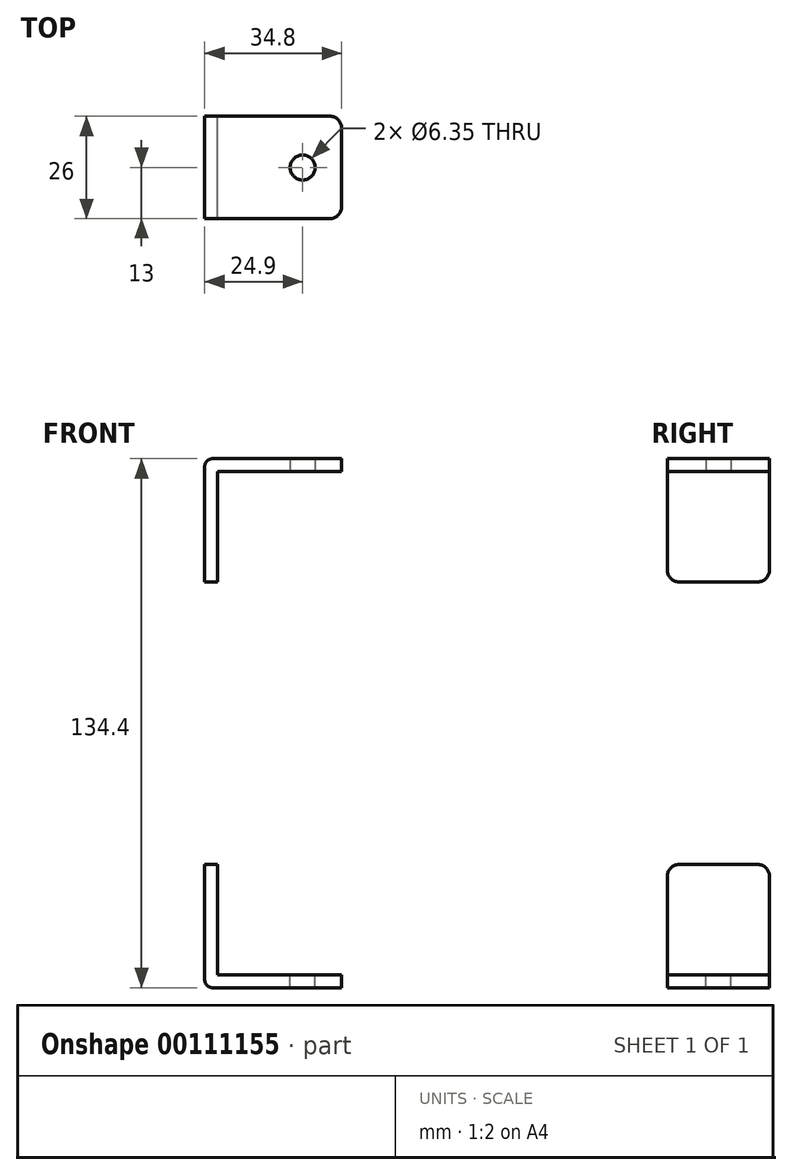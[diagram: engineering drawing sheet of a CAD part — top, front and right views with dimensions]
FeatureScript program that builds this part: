
annotation { "Feature Type Name" : "Feature", "Feature Type Description" : "" }
export const myFeature = defineFeature(function(context is Context, id is Id, definition is map)
    precondition{}
    {
        {
            var Q0;
            Q0=qCreatedBy(makeId("Top.planeOp"),FACE);
            var sketch = newSketch(context, id + "F0", { "sketchPlane" : qUnion([Q0])});
            skLineSegment(sketch, "E0.rect.bottom", {"start": v(15.75, 13) * mm, "end": v(-15.75, 13) * mm});
            skLineSegment(sketch, "E0.rect.top", {"start": v(15.75, -13) * mm, "end": v(-15.75, -13) * mm});
            skLineSegment(sketch, "E0.rect.left", {"start": v(15.75, 13) * mm, "end": v(15.75, -13) * mm});
            skLineSegment(sketch, "E0.rect.right", {"start": v(-15.75, 13) * mm, "end": v(-15.75, -13) * mm});
            skPoint(sketch, "E0.rect.middle", {"position": v(0, 0) * mm});
            skLineSegment(sketch, "E1.bottom", {"start": v(-15.75, 13) * mm, "end": v(-19.05, 13) * mm});
            skLineSegment(sketch, "E1.top", {"start": v(-15.75, -13) * mm, "end": v(-19.05, -13) * mm});
            skLineSegment(sketch, "E1.right", {"start": v(-19.05, 13) * mm, "end": v(-19.05, -13) * mm});
            skLineSegment(sketch, "E2", {"start": v(-15.75, 0) * mm, "end": v(15.75, 0) * mm, "construction": true});
            skSolve(sketch);
        }
        {
            var Q0;
            Q0=makeQuery(id+"F0.imprint","IMPRINT",FACE,{"disambiguationData":[TD([[makeQuery(id+"F0.imprint","IMPRINT",EDGE,{"derivedFrom":sQuery(id+"F0.wireOp",EDGE,"E1.bottom")}),1.0]])]});
            var Q1;
            Q1=makeQuery(id+"F0.imprint","IMPRINT",FACE,{"disambiguationData":[TD([[makeQuery(id+"F0.imprint","IMPRINT",EDGE,{"derivedFrom":sQuery(id+"F0.wireOp",EDGE,"E0.rect.bottom")}),1.0]])]});
            extrude(context, id + "F1", {"entities" : qUnion([Q0, Q1]), "oppositeDirection" : true, "depth" : 3.3 * mm});
        }
        {
            var Q0;
            Q0=makeQuery(id+"F0.imprint","IMPRINT",FACE,{"disambiguationData":[TD([[makeQuery(id+"F0.imprint","IMPRINT",EDGE,{"derivedFrom":sQuery(id+"F0.wireOp",EDGE,"E1.bottom")}),1.0]])]});
            extrude(context, id + "F2", {"entities" : qUnion([Q0]), "operationType" : NewBodyOperationType.ADD, "depth" : 28 * mm});
        }
        {
            var Q0;
            Q0=makeQuery(id+"F0.imprint","IMPRINT",FACE,{"disambiguationData":[TD([[makeQuery(id+"F0.imprint","IMPRINT",EDGE,{"derivedFrom":sQuery(id+"F0.wireOp",EDGE,"E0.rect.bottom")}),1.0]])]});
            var sketch = newSketch(context, id + "F3", { "sketchPlane" : qUnion([Q0])});
            skCircle(sketch, "E3", {"center": v(5.85, 0) * mm, "radius": 3.18 * mm});
            skSolve(sketch);
        }
        {
            var Q0;
            Q0=makeQuery(id+"F3.imprint","IMPRINT",FACE,{"disambiguationData":[TD([[makeQuery(id+"F3.imprint","IMPRINT",EDGE,{"derivedFrom":sQuery(id+"F3.wireOp",EDGE,"E3")}),1.0]])]});
            extrude(context, id + "F4", {"entities" : qUnion([Q0]), "operationType" : NewBodyOperationType.REMOVE, "endBound" : BoundingType.THROUGH_ALL, "oppositeDirection" : true, "depth" : 25 * mm});
        }
        {
            var Q0;
            Q0=makeQuery(id+"F1.opExtrude","SWEPT_EDGE",EDGE,{"disambiguationData":[OSD([sQuery(id+"F0.wireOp",EDGE,"E0.rect.top"),sQuery(id+"F0.wireOp",EDGE,"E0.rect.left")])]});
            var Q1;
            Q1=makeQuery(id+"F1.opExtrude","SWEPT_EDGE",EDGE,{"disambiguationData":[OSD([sQuery(id+"F0.wireOp",EDGE,"E0.rect.bottom"),sQuery(id+"F0.wireOp",EDGE,"E0.rect.left")])]});
            var Q2;
            Q2=makeQuery(id+"F2.opExtrude","CAP_EDGE",EDGE,{"disambiguationData":[OSD([sQuery(id+"F0.wireOp",EDGE,"E1.top")])],"isStart":false});
            var Q3;
            Q3=makeQuery(id+"F2.opExtrude","CAP_EDGE",EDGE,{"disambiguationData":[OSD([sQuery(id+"F0.wireOp",EDGE,"E1.bottom")])],"isStart":false});
            fillet(context, id + "F5", {"entities" : qUnion([Q0, Q1, Q2, Q3]), "radius" : 3 * mm, "tangentPropagation" : true, "allowEdgeOverflow" : false});
        }
        {
            var Q0;
            Q0=makeQuery(id+"F2.opExtrude","CAP_EDGE",EDGE,{"disambiguationData":[OSD([sQuery(id+"F0.wireOp",EDGE,"E0.rect.right")])],"isStart":true});
            var Q1;
            Q1=makeQuery(id+"F1.opExtrude","CAP_EDGE",EDGE,{"disambiguationData":[OSD([sQuery(id+"F0.wireOp",EDGE,"E1.right")])],"isStart":false});
            fillet(context, id + "F6", {"entities" : qUnion([Q0, Q1]), "radius" : 2 * mm, "tangentPropagation" : true, "allowEdgeOverflow" : false});
        }
        {
            var Q0;
            Q0=makeQuery(id+"F1.opExtrude","SWEPT_FACE",FACE,{"disambiguationData":[OSD([sQuery(id+"F0.wireOp",EDGE,"E0.rect.left")])]});
            var sketch = newSketch(context, id + "F7", { "sketchPlane" : qUnion([Q0])});
            skLineSegment(sketch, "E4", {"start": v(0, 0) * mm, "end": v(0, 127.8) * mm, "construction": true});
            skSolve(sketch);
        }
        {
            var Q0;
            Q0=makeQuery(id+"F1.opExtrude","SWEPT_BODY",BODY,{"disambiguationData":[OSD([sQuery(id+"F0.wireOp",EDGE,"E0.rect.bottom"),sQuery(id+"F0.wireOp",EDGE,"E0.rect.top"),sQuery(id+"F0.wireOp",EDGE,"E0.rect.left"),sQuery(id+"F0.wireOp",EDGE,"E1.bottom"),sQuery(id+"F0.wireOp",EDGE,"E1.top"),sQuery(id+"F0.wireOp",EDGE,"E1.right")])]});
            var Q1;
            Q1=sQuery(id+"F7.wireOp",EDGE,"E4");
            var Q2;
            Q2=sQuery(id+"F7.wireOp",EDGE,"E4");
            transform(context, id + "F8", {"entities" : qUnion([Q0]), "transformType" : TransformType.TRANSLATION_ENTITY, "oppositeDirectionEntity" : false, "transformLine" : qUnion([Q1]), "makeCopy" : true});
        }
        {
            var Q0;
            Q0=makeQuery(id+"F8.opPattern","COPY",FACE,{"derivedFrom":makeQuery(id+"F1.opExtrude","CAP_FACE",FACE,{"disambiguationData":[OSD([sQuery(id+"F0.wireOp",EDGE,"E0.rect.bottom"),sQuery(id+"F0.wireOp",EDGE,"E0.rect.top"),sQuery(id+"F0.wireOp",EDGE,"E0.rect.left"),sQuery(id+"F0.wireOp",EDGE,"E1.bottom"),sQuery(id+"F0.wireOp",EDGE,"E1.top"),sQuery(id+"F0.wireOp",EDGE,"E1.right")])],"isStart":true}),"instanceName":"1"});
            var sketch = newSketch(context, id + "F9", { "sketchPlane" : qUnion([Q0])});
            skLineSegment(sketch, "E5", {"start": v(15.75, 0) * mm, "end": v(5.85, 0) * mm, "construction": true});
            skSolve(sketch);
        }
        {
            var Q0;
            Q0=makeQuery(id+"F8.opPattern","COPY",BODY,{"derivedFrom":makeQuery(id+"F1.opExtrude","SWEPT_BODY",BODY,{"disambiguationData":[OSD([sQuery(id+"F0.wireOp",EDGE,"E0.rect.bottom"),sQuery(id+"F0.wireOp",EDGE,"E0.rect.top"),sQuery(id+"F0.wireOp",EDGE,"E0.rect.left"),sQuery(id+"F0.wireOp",EDGE,"E1.bottom"),sQuery(id+"F0.wireOp",EDGE,"E1.top"),sQuery(id+"F0.wireOp",EDGE,"E1.right")])]}),"instanceName":"1"});
            var Q1;
            Q1=sQuery(id+"F9.wireOp",EDGE,"E5");
            transform(context, id + "F10", {"entities" : qUnion([Q0]), "transformType" : TransformType.ROTATION, "transformAxis" : qUnion([Q1]), "angle" : 180 * degree, "makeCopy" : false});
        }
    });
